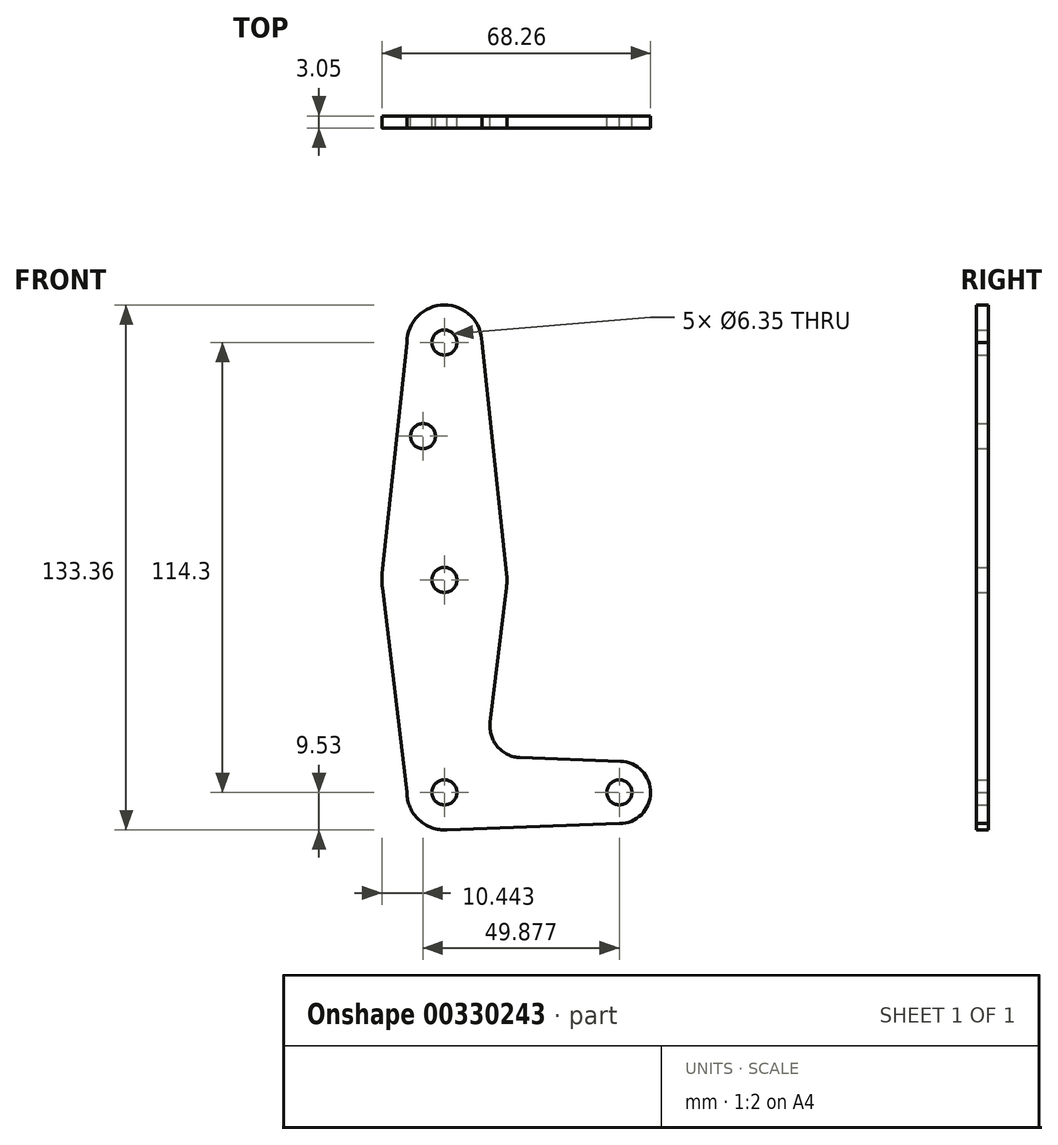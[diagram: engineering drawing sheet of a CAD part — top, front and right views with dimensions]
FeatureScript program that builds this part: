
annotation { "Feature Type Name" : "Feature", "Feature Type Description" : "" }
export const myFeature = defineFeature(function(context is Context, id is Id, definition is map)
    precondition{}
    {
        {
            var Q0;
            Q0=qCreatedBy(makeId("Front.planeOp"),FACE);
            var sketch = newSketch(context, id + "F0", { "sketchPlane" : qUnion([Q0])});
            skLineSegment(sketch, "E0", {"start": v(0, 0) * mm, "end": v(0, 114.3) * mm, "construction": true});
            skLineSegment(sketch, "E1", {"start": v(0, 0) * mm, "end": v(44.45, 0) * mm, "construction": true});
            skCircle(sketch, "E2", {"center": v(0, 114.3) * mm, "radius": 9.53 * mm});
            skCircle(sketch, "E3", {"center": v(0, 0) * mm, "radius": 9.53 * mm});
            skCircle(sketch, "E4", {"center": v(0, 53.97) * mm, "radius": 15.88 * mm});
            skCircle(sketch, "E5", {"center": v(44.45, 0) * mm, "radius": 7.94 * mm});
            skLineSegment(sketch, "E6", {"start": v(19.26, 8.84) * mm, "end": v(44.73, 7.93) * mm});
            skLineSegment(sketch, "E7", {"start": v(0, -9.53) * mm, "end": v(44.45, -7.94) * mm});
            skLineSegment(sketch, "E8", {"start": v(-9.53, 114.3) * mm, "end": v(-15.79, 55.66) * mm});
            skLineSegment(sketch, "E9", {"start": v(9.52, 114.3) * mm, "end": v(15.79, 55.66) * mm});
            skLineSegment(sketch, "E10", {"start": v(11.65, 17.73) * mm, "end": v(15.76, 52.09) * mm});
            skLineSegment(sketch, "E11", {"start": v(-9.53, 0) * mm, "end": v(-15.76, 52.09) * mm});
            skCircle(sketch, "E12", {"center": v(0, 114.3) * mm, "radius": 3.18 * mm});
            skCircle(sketch, "E13", {"center": v(0, 53.97) * mm, "radius": 3.18 * mm});
            skCircle(sketch, "E14", {"center": v(0, 0) * mm, "radius": 3.18 * mm});
            skCircle(sketch, "E15", {"center": v(-5.43, 90.5) * mm, "radius": 3.18 * mm});
            skCircle(sketch, "E16", {"center": v(44.45, 0) * mm, "radius": 3.18 * mm});
            skArc(sketch, "E17.filletArc", {"start": v(11.65, 17.73) * mm, "mid": v(13.5, 11.61) * mm, "end": v(19.26, 8.84) * mm});
            skSolve(sketch);
        }
        {
            var Q0;
            Q0 = qSketchRegion(id + "F0", true);
            extrude(context, id + "F1", {"entities" : qUnion([Q0]), "depth" : 3.05 * mm});
        }
    });
